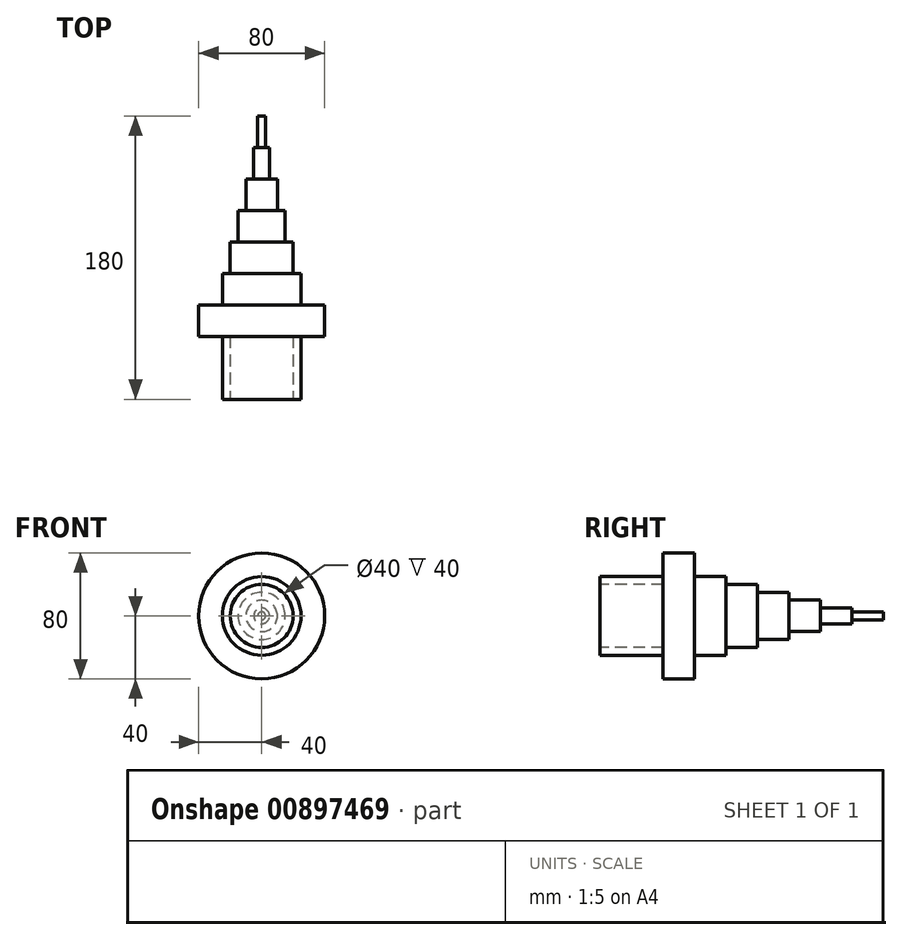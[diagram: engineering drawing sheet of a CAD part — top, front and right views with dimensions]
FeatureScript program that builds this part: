
annotation { "Feature Type Name" : "Feature", "Feature Type Description" : "" }
export const myFeature = defineFeature(function(context is Context, id is Id, definition is map)
    precondition{}
    {
        {
            var Q0;
            Q0=qCreatedBy(makeId("Front.planeOp"),FACE);
            var sketch = newSketch(context, id + "F0", { "sketchPlane" : qUnion([Q0])});
            skCircle(sketch, "E0", {"center": v(0, 0) * mm, "radius": 40 * mm});
            skSolve(sketch);
        }
        {
            var Q0;
            Q0=makeQuery(id+"F0.imprint","IMPRINT",FACE,{"disambiguationData":[TD([[makeQuery(id+"F0.imprint","IMPRINT",EDGE,{"derivedFrom":sQuery(id+"F0.wireOp",EDGE,"E0")}),1.0]])]});
            extrude(context, id + "F1", {"entities" : qUnion([Q0]), "depth" : 20 * mm, "offsetDistance" : 25.4 * mm});
        }
        {
            var Q0;
            Q0=makeQuery(id+"F1.opExtrude","CAP_FACE",FACE,{"disambiguationData":[OSD([sQuery(id+"F0.wireOp",EDGE,"E0")])],"isStart":false});
            var sketch = newSketch(context, id + "F2", { "sketchPlane" : qUnion([Q0])});
            skCircle(sketch, "E1", {"center": v(0, 0) * mm, "radius": 25 * mm});
            skSolve(sketch);
        }
        {
            var Q0;
            Q0=makeQuery(id+"F2.imprint","IMPRINT",FACE,{"disambiguationData":[TD([[makeQuery(id+"F2.imprint","IMPRINT",EDGE,{"derivedFrom":sQuery(id+"F2.wireOp",EDGE,"E1")}),1.0]])]});
            extrude(context, id + "F3", {"entities" : qUnion([Q0]), "operationType" : NewBodyOperationType.ADD, "depth" : 40 * mm, "offsetDistance" : 25.4 * mm});
        }
        {
            var Q0;
            Q0=makeQuery(id+"F1.opExtrude","CAP_FACE",FACE,{"disambiguationData":[OSD([sQuery(id+"F0.wireOp",EDGE,"E0")])],"isStart":true});
            var sketch = newSketch(context, id + "F4", { "sketchPlane" : qUnion([Q0])});
            skCircle(sketch, "E2", {"center": v(0, 0) * mm, "radius": 25 * mm});
            skSolve(sketch);
        }
        {
            var Q0;
            Q0=makeQuery(id+"F4.imprint","IMPRINT",FACE,{"disambiguationData":[TD([[makeQuery(id+"F4.imprint","IMPRINT",EDGE,{"derivedFrom":sQuery(id+"F4.wireOp",EDGE,"E2")}),1.0]])]});
            extrude(context, id + "F5", {"entities" : qUnion([Q0]), "operationType" : NewBodyOperationType.ADD, "depth" : 20 * mm, "offsetDistance" : 25.4 * mm});
        }
        {
            var Q0;
            Q0=makeQuery(id+"F5.opExtrude","CAP_FACE",FACE,{"disambiguationData":[OSD([sQuery(id+"F4.wireOp",EDGE,"E2")])],"isStart":false});
            var sketch = newSketch(context, id + "F6", { "sketchPlane" : qUnion([Q0])});
            skCircle(sketch, "E3", {"center": v(0, 0) * mm, "radius": 20 * mm});
            skSolve(sketch);
        }
        {
            var Q0;
            Q0=makeQuery(id+"F6.imprint","IMPRINT",FACE,{"disambiguationData":[TD([[makeQuery(id+"F6.imprint","IMPRINT",EDGE,{"derivedFrom":sQuery(id+"F6.wireOp",EDGE,"E3")}),1.0]])]});
            extrude(context, id + "F7", {"entities" : qUnion([Q0]), "operationType" : NewBodyOperationType.ADD, "depth" : 20 * mm, "offsetDistance" : 25.4 * mm});
        }
        {
            var Q0;
            Q0=makeQuery(id+"F7.opExtrude","CAP_FACE",FACE,{"disambiguationData":[OSD([sQuery(id+"F6.wireOp",EDGE,"E3")])],"isStart":false});
            var sketch = newSketch(context, id + "F8", { "sketchPlane" : qUnion([Q0])});
            skCircle(sketch, "E4", {"center": v(0, 0) * mm, "radius": 15 * mm});
            skSolve(sketch);
        }
        {
            var Q0;
            Q0=makeQuery(id+"F8.imprint","IMPRINT",FACE,{"disambiguationData":[TD([[makeQuery(id+"F8.imprint","IMPRINT",EDGE,{"derivedFrom":sQuery(id+"F8.wireOp",EDGE,"E4")}),1.0]])]});
            extrude(context, id + "F9", {"entities" : qUnion([Q0]), "operationType" : NewBodyOperationType.ADD, "depth" : 20 * mm, "offsetDistance" : 25.4 * mm});
        }
        {
            var Q0;
            Q0=makeQuery(id+"F9.opExtrude","CAP_FACE",FACE,{"disambiguationData":[OSD([sQuery(id+"F8.wireOp",EDGE,"E4")])],"isStart":false});
            var sketch = newSketch(context, id + "F10", { "sketchPlane" : qUnion([Q0])});
            skCircle(sketch, "E5", {"center": v(0, 0) * mm, "radius": 20 * mm});
            skSolve(sketch);
        }
        {
            var Q0;
            Q0=makeQuery(id+"F10.imprint","IMPRINT",FACE,{"disambiguationData":[TD([[makeQuery(id+"F10.imprint","IMPRINT",EDGE,{"derivedFrom":makeQuery(id+"F9.opExtrude","CAP_EDGE",EDGE,{"disambiguationData":[OSD([sQuery(id+"F8.wireOp",EDGE,"E4")])],"isStart":false})}),1.0]])]});
            var sketch = newSketch(context, id + "F11", { "sketchPlane" : qUnion([Q0])});
            skCircle(sketch, "E6", {"center": v(0, 0) * mm, "radius": 10 * mm});
            skSolve(sketch);
        }
        {
            var Q0;
            Q0=makeQuery(id+"F11.imprint","IMPRINT",FACE,{"disambiguationData":[TD([[makeQuery(id+"F11.imprint","IMPRINT",EDGE,{"derivedFrom":sQuery(id+"F11.wireOp",EDGE,"E6")}),1.0]])]});
            extrude(context, id + "F12", {"entities" : qUnion([Q0]), "operationType" : NewBodyOperationType.ADD, "depth" : 20 * mm, "offsetDistance" : 25.4 * mm});
        }
        {
            var Q0;
            Q0=makeQuery(id+"F12.opExtrude","CAP_FACE",FACE,{"disambiguationData":[OSD([sQuery(id+"F11.wireOp",EDGE,"E6")])],"isStart":false});
            var sketch = newSketch(context, id + "F13", { "sketchPlane" : qUnion([Q0])});
            skCircle(sketch, "E7", {"center": v(0, 0) * mm, "radius": 5 * mm});
            skSolve(sketch);
        }
        {
            var Q0;
            Q0=makeQuery(id+"F13.imprint","IMPRINT",FACE,{"disambiguationData":[TD([[makeQuery(id+"F13.imprint","IMPRINT",EDGE,{"derivedFrom":sQuery(id+"F13.wireOp",EDGE,"E7")}),1.0]])]});
            extrude(context, id + "F14", {"entities" : qUnion([Q0]), "operationType" : NewBodyOperationType.ADD, "depth" : 20 * mm, "offsetDistance" : 25.4 * mm});
        }
        {
            var Q0;
            Q0=makeQuery(id+"F14.opExtrude","CAP_FACE",FACE,{"disambiguationData":[OSD([sQuery(id+"F13.wireOp",EDGE,"E7")])],"isStart":false});
            var sketch = newSketch(context, id + "F15", { "sketchPlane" : qUnion([Q0])});
            skCircle(sketch, "E8", {"center": v(0, 0) * mm, "radius": 2.5 * mm});
            skSolve(sketch);
        }
        {
            var Q0;
            Q0=makeQuery(id+"F15.imprint","IMPRINT",FACE,{"disambiguationData":[TD([[makeQuery(id+"F15.imprint","IMPRINT",EDGE,{"derivedFrom":sQuery(id+"F15.wireOp",EDGE,"E8")}),1.0]])]});
            extrude(context, id + "F16", {"entities" : qUnion([Q0]), "operationType" : NewBodyOperationType.ADD, "depth" : 20 * mm, "offsetDistance" : 25.4 * mm});
        }
        {
            var Q0;
            Q0=makeQuery(id+"F3.opExtrude","CAP_FACE",FACE,{"disambiguationData":[OSD([sQuery(id+"F2.wireOp",EDGE,"E1")])],"isStart":false});
            var sketch = newSketch(context, id + "F17", { "sketchPlane" : qUnion([Q0])});
            skCircle(sketch, "E9", {"center": v(0, 0) * mm, "radius": 20 * mm});
            skSolve(sketch);
        }
        {
            var Q0;
            Q0=makeQuery(id+"F17.imprint","IMPRINT",FACE,{"disambiguationData":[TD([[makeQuery(id+"F17.imprint","IMPRINT",EDGE,{"derivedFrom":sQuery(id+"F17.wireOp",EDGE,"E9")}),1.0]])]});
            extrude(context, id + "F18", {"entities" : qUnion([Q0]), "operationType" : NewBodyOperationType.REMOVE, "oppositeDirection" : true, "depth" : 40 * mm, "offsetDistance" : 25.4 * mm});
        }
    });
